# Revit family: 4LSS24238A75FTB.V2,A2FTB.V2
name_source: partatom
category: Plumbing Fixtures
revit_build: Autodesk Revit LT 2017 (Build: 20160225_1515(x64)
units: mm (PartAtom-declared; Revit-internal decimal feet)

## family parameters
Always vertical = Yes
Cut with Voids When Loaded = No
OmniClass Number = 23.45.05.14.17
OmniClass Title = Showers
Part Type = Normal
Room Calculation Point = No
Round Connector Dimension = Use Diameter
Shared = No
Work Plane-Based = No

## types (2) — shared parameters
Assembly Code = D2010710
Description = Trench Drain, Smooth Tile, Bevelled Threshold
Keynote = 22 40 00.B3
Manufacturer = Best Bath Systems, Inc.
Seat Height = 18"
Type Comments = ADA Compliant
URL = http://www.bestbath.com
Unit Width = 38 1/2"

## per-type parameters (varying)
| type | Threshold Height | Unit Height |
| 4LSS24238A75FTB.V2 | 3/4" | 81 1/4" |
| 4LSS24238A2FTB.V2 | 2" | 82 1/2" |

note: column(s) folded — value = type name in every type: Model

## geometry (parser evidence)
native form markers: Blend x26, Sweep x12
no freeform markers — native parametric forms only
